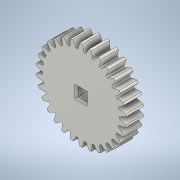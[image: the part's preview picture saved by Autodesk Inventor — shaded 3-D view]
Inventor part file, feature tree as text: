
AUTODESK INVENTOR PART (.ipt)
format: ipt  version: 2022 (Build 260153000, 153)  size: 587,264 bytes
history: native  units: mm (DEFAULTED — no unit token found)
features: plane x3, other x3, sketch x3, extrude x2, chamfer x1
ambient origin geometry x8: Origin, YZ Plane, XZ Plane, XY Plane, X Axis, Y Axis, Z Axis, Center Point
bodies: Solid1 (feature_tree)
feature tree (12):
  extrude  "Extrusion1"  Depth=6.35mm TaperAngle=0.0deg
  plane  "Work Plane1"
  plane  "Work Plane2"
  plane  "Work Plane3"
  other  "Spur Gear"
  extrude  "Extrusion2"  Depth=76.2mm TaperAngle=0.0deg
  chamfer  "Chamfer1"  Distance=1.047198mm
  sketch  "Sketch1"  dims[d0=31.912126mm d1=6.35mm d2=0.0mm]
  sketch  "Sketch2"  dims[d3=30.0mm d4=76.2mm d5=0.0mm d6=0.0mm d7=1.047198mm]
  other  "Srf1"
  sketch  "Sketch3"  dims[d9=0.0mm d14=0.0mm d15=25.4mm d16=0.0mm d17=0.0mm d18=0.0mm d19=25.4mm d20=3.325mm d21=0.0mm d22=0.0mm d23=0.6mm d24=3.175mm d25=45.0deg]
  other  "Pitch Diameter"
